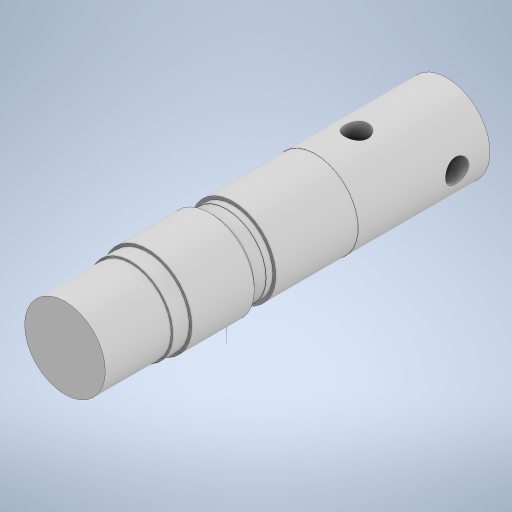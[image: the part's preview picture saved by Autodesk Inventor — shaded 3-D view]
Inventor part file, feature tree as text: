
AUTODESK INVENTOR PART (.ipt)
format: ipt  version: 2024 (Build 280153000, 153)  size: 318,464 bytes
history: native  units: mm
features: sketch x5, extrude x2, plane x1, revolve x1, chamfer x1
ambient origin geometry x8: Origin, YZ Plane, XZ Plane, XY Plane, X Axis, Y Axis, Z Axis, Center Point
bodies: Body1 (feature_tree)
feature tree (10):
  sketch  "Sketch1"  dims[d2=40.0mm d4=8.0mm]
  plane  "Work Plane1"
  sketch  "Sketch3"  dims[d5=4.0mm d6=50.0mm]
  sketch  "Sketch4"  dims[d16=10.0mm d17=15.0mm]
  revolve  "Revolution1"  [1 undecoded]
  extrude  "Extrusion5"  Depth=4.0mm
  extrude  "Extrusion6"  Depth=10.0mm
  chamfer  "Chamfer3"  Angle=90.0deg  [1 undecoded]
  sketch  "Sketch5"  dims[d22=14.0mm]
  sketch  "Sketch6"  dims[d28=14.0mm d31=90.0deg d34=20.0mm d35=45.0mm d36=0.0mm d37=0.0mm d38=35.0mm d39=30.0mm d40=0.0mm d41=0.0mm d48=2.0mm d49=2.0mm d50=45.0deg d66=79.0mm d67=114.0mm d71=27.0mm d78=24.0mm d82=4.0mm d83=50.0mm d84=24.2mm d85=26.1mm d86=80.0mm d88=25.5mm d89=26.0mm d90=40.0mm d92=24.5mm d20=0.5mm d21=0.872665mm d23=0.872665mm d32=0.872665mm]
note: 2 required parameter values undecoded (feature->parameter linkage not recoverable at this tier; creation-order binding heuristic only, values carry confidence <= 0.55)